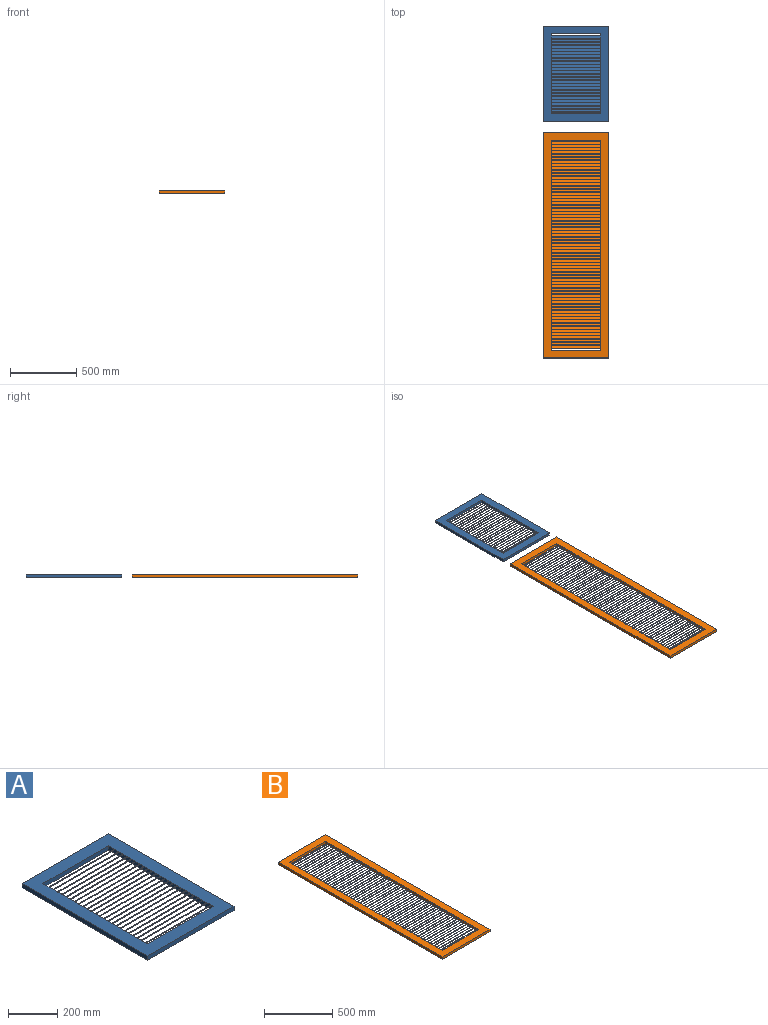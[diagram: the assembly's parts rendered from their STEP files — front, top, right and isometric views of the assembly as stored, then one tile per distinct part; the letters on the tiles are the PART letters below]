
ASSEMBLY  parts=2 mates=2
PART A: 106 faces, bbox 494x720x21 mm
  f0: plane 600x21mm, normal (1,0,0), area 10776mm2, adj f2,f7,f8,f9,f10,f11,f12,f13
  f1: plane 600x21mm, normal (-1,0,0), area 10776mm2, adj f2,f7,f8,f9,f10,f11,f12,f13
  f2: plane 374x21mm, normal (0,-1,0), area 7854mm2, adj f0,f1,f8,f9
  f3: plane 494x21mm, normal (0,1,0), area 10374mm2, adj f4,f6,f8,f9
  f4: plane 720x21mm, normal (-1,0,0), area 15120mm2, adj f3,f5,f8,f9
  f5: plane 494x21mm, normal (0,-1,0), area 10374mm2, adj f4,f6,f8,f9
  f6: plane 720x21mm, normal (1,0,0), area 15120mm2, adj f3,f5,f8,f9
  f7: plane 374x21mm, normal (0,1,0), area 7854mm2, adj f0,f1,f8,f9
  f8: plane 720x494mm, normal (0,0,1), area 131280mm2, adj f0,f1,f2,f3,f4,f5,f6,f7
  f9: plane 720x494mm, normal (0,0,-1), area 131280mm2, adj f0,f1,f2,f3,f4,f5,f6,f7
  f10: plane 374x19mm, normal (0,-0.71,-0.71), area 10049.4mm2, adj f0,f1,f11,f13
  f11: plane 374x4mm, normal (0,0,-1), area 1496mm2, adj f0,f1,f10,f12
  f12: plane 374x19mm, normal (0,0.71,0.71), area 10049.4mm2, adj f0,f1,f11,f13
  f13: plane 374x4mm, normal (0,0,1), area 1496mm2, adj f0,f1,f10,f12
  f14: plane 374x19mm, normal (0,-0.71,-0.71), area 10049.4mm2, adj f0,f1,f15,f17
  f15: plane 374x4mm, normal (0,0,-1), area 1496mm2, adj f0,f1,f14,f16
  f16: plane 374x19mm, normal (0,0.71,0.71), area 10049.4mm2, adj f0,f1,f15,f17
  f17: plane 374x4mm, normal (0,0,1), area 1496mm2, adj f0,f1,f14,f16
  f18: plane 374x19mm, normal (0,-0.71,-0.71), area 10049.4mm2, adj f0,f1,f19,f21
  f19: plane 374x4mm, normal (0,0,-1), area 1496mm2, adj f0,f1,f18,f20
  f20: plane 374x19mm, normal (0,0.71,0.71), area 10049.4mm2, adj f0,f1,f19,f21
  f21: plane 374x4mm, normal (0,0,1), area 1496mm2, adj f0,f1,f18,f20
  f22: plane 374x19mm, normal (0,-0.71,-0.71), area 10049.4mm2, adj f0,f1,f23,f25
  f23: plane 374x4mm, normal (0,0,-1), area 1496mm2, adj f0,f1,f22,f24
  f24: plane 374x19mm, normal (0,0.71,0.71), area 10049.4mm2, adj f0,f1,f23,f25
  f25: plane 374x4mm, normal (0,0,1), area 1496mm2, adj f0,f1,f22,f24
  f26: plane 374x19mm, normal (0,-0.71,-0.71), area 10049.4mm2, adj f0,f1,f27,f29
  f27: plane 374x4mm, normal (0,0,-1), area 1496mm2, adj f0,f1,f26,f28
  f28: plane 374x19mm, normal (0,0.71,0.71), area 10049.4mm2, adj f0,f1,f27,f29
  f29: plane 374x4mm, normal (0,0,1), area 1496mm2, adj f0,f1,f26,f28
  f30: plane 374x19mm, normal (0,-0.71,-0.71), area 10049.4mm2, adj f0,f1,f31,f33
  f31: plane 374x4mm, normal (0,0,-1), area 1496mm2, adj f0,f1,f30,f32
  f32: plane 374x19mm, normal (0,0.71,0.71), area 10049.4mm2, adj f0,f1,f31,f33
  f33: plane 374x4mm, normal (0,0,1), area 1496mm2, adj f0,f1,f30,f32
  f34: plane 374x19mm, normal (0,-0.71,-0.71), area 10049.4mm2, adj f0,f1,f35,f37
  f35: plane 374x4mm, normal (0,0,-1), area 1496mm2, adj f0,f1,f34,f36
  f36: plane 374x19mm, normal (0,0.71,0.71), area 10049.4mm2, adj f0,f1,f35,f37
  f37: plane 374x4mm, normal (0,0,1), area 1496mm2, adj f0,f1,f34,f36
  f38: plane 374x19mm, normal (0,-0.71,-0.71), area 10049.4mm2, adj f0,f1,f39,f41
  f39: plane 374x4mm, normal (0,0,-1), area 1496mm2, adj f0,f1,f38,f40
  f40: plane 374x19mm, normal (0,0.71,0.71), area 10049.4mm2, adj f0,f1,f39,f41
  f41: plane 374x4mm, normal (0,0,1), area 1496mm2, adj f0,f1,f38,f40
  f42: plane 374x19mm, normal (0,-0.71,-0.71), area 10049.4mm2, adj f0,f1,f43,f45
  f43: plane 374x4mm, normal (0,0,-1), area 1496mm2, adj f0,f1,f42,f44
  f44: plane 374x19mm, normal (0,0.71,0.71), area 10049.4mm2, adj f0,f1,f43,f45
  f45: plane 374x4mm, normal (0,0,1), area 1496mm2, adj f0,f1,f42,f44
  f46: plane 374x19mm, normal (0,-0.71,-0.71), area 10049.4mm2, adj f0,f1,f47,f49
  f47: plane 374x4mm, normal (0,0,-1), area 1496mm2, adj f0,f1,f46,f48
  f48: plane 374x19mm, normal (0,0.71,0.71), area 10049.4mm2, adj f0,f1,f47,f49
  f49: plane 374x4mm, normal (0,0,1), area 1496mm2, adj f0,f1,f46,f48
  f50: plane 374x19mm, normal (0,-0.71,-0.71), area 10049.4mm2, adj f0,f1,f51,f53
  f51: plane 374x4mm, normal (0,0,-1), area 1496mm2, adj f0,f1,f50,f52
  f52: plane 374x19mm, normal (0,0.71,0.71), area 10049.4mm2, adj f0,f1,f51,f53
  f53: plane 374x4mm, normal (0,0,1), area 1496mm2, adj f0,f1,f50,f52
  f54: plane 374x19mm, normal (0,-0.71,-0.71), area 10049.4mm2, adj f0,f1,f55,f57
  f55: plane 374x4mm, normal (0,0,-1), area 1496mm2, adj f0,f1,f54,f56
  f56: plane 374x19mm, normal (0,0.71,0.71), area 10049.4mm2, adj f0,f1,f55,f57
  f57: plane 374x4mm, normal (0,0,1), area 1496mm2, adj f0,f1,f54,f56
  f58: plane 374x19mm, normal (0,-0.71,-0.71), area 10049.4mm2, adj f0,f1,f59,f61
  f59: plane 374x4mm, normal (0,0,-1), area 1496mm2, adj f0,f1,f58,f60
  f60: plane 374x19mm, normal (0,0.71,0.71), area 10049.4mm2, adj f0,f1,f59,f61
  f61: plane 374x4mm, normal (0,0,1), area 1496mm2, adj f0,f1,f58,f60
  f62: plane 374x19mm, normal (0,-0.71,-0.71), area 10049.4mm2, adj f0,f1,f63,f65
  f63: plane 374x4mm, normal (0,0,-1), area 1496mm2, adj f0,f1,f62,f64
  f64: plane 374x19mm, normal (0,0.71,0.71), area 10049.4mm2, adj f0,f1,f63,f65
  f65: plane 374x4mm, normal (0,0,1), area 1496mm2, adj f0,f1,f62,f64
  f66: plane 374x19mm, normal (0,-0.71,-0.71), area 10049.4mm2, adj f0,f1,f67,f69
  f67: plane 374x4mm, normal (0,0,-1), area 1496mm2, adj f0,f1,f66,f68
  f68: plane 374x19mm, normal (0,0.71,0.71), area 10049.4mm2, adj f0,f1,f67,f69
  f69: plane 374x4mm, normal (0,0,1), area 1496mm2, adj f0,f1,f66,f68
  f70: plane 374x19mm, normal (0,-0.71,-0.71), area 10049.4mm2, adj f0,f1,f71,f73
  f71: plane 374x4mm, normal (0,0,-1), area 1496mm2, adj f0,f1,f70,f72
  f72: plane 374x19mm, normal (0,0.71,0.71), area 10049.4mm2, adj f0,f1,f71,f73
  f73: plane 374x4mm, normal (0,0,1), area 1496mm2, adj f0,f1,f70,f72
  f74: plane 374x19mm, normal (0,-0.71,-0.71), area 10049.4mm2, adj f0,f1,f75,f77
  f75: plane 374x4mm, normal (0,0,-1), area 1496mm2, adj f0,f1,f74,f76
  f76: plane 374x19mm, normal (0,0.71,0.71), area 10049.4mm2, adj f0,f1,f75,f77
  f77: plane 374x4mm, normal (0,0,1), area 1496mm2, adj f0,f1,f74,f76
  f78: plane 374x19mm, normal (0,-0.71,-0.71), area 10049.4mm2, adj f0,f1,f79,f81
  f79: plane 374x4mm, normal (0,0,-1), area 1496mm2, adj f0,f1,f78,f80
  f80: plane 374x19mm, normal (0,0.71,0.71), area 10049.4mm2, adj f0,f1,f79,f81
  f81: plane 374x4mm, normal (0,0,1), area 1496mm2, adj f0,f1,f78,f80
  f82: plane 374x19mm, normal (0,-0.71,-0.71), area 10049.4mm2, adj f0,f1,f83,f85
  f83: plane 374x4mm, normal (0,0,-1), area 1496mm2, adj f0,f1,f82,f84
  f84: plane 374x19mm, normal (0,0.71,0.71), area 10049.4mm2, adj f0,f1,f83,f85
  f85: plane 374x4mm, normal (0,0,1), area 1496mm2, adj f0,f1,f82,f84
  f86: plane 374x19mm, normal (0,-0.71,-0.71), area 10049.4mm2, adj f0,f1,f87,f89
  f87: plane 374x4mm, normal (0,0,-1), area 1496mm2, adj f0,f1,f86,f88
  f88: plane 374x19mm, normal (0,0.71,0.71), area 10049.4mm2, adj f0,f1,f87,f89
  f89: plane 374x4mm, normal (0,0,1), area 1496mm2, adj f0,f1,f86,f88
  f90: plane 374x19mm, normal (0,-0.71,-0.71), area 10049.4mm2, adj f0,f1,f91,f93
  f91: plane 374x4mm, normal (0,0,-1), area 1496mm2, adj f0,f1,f90,f92
  f92: plane 374x19mm, normal (0,0.71,0.71), area 10049.4mm2, adj f0,f1,f91,f93
  f93: plane 374x4mm, normal (0,0,1), area 1496mm2, adj f0,f1,f90,f92
  f94: plane 374x19mm, normal (0,-0.71,-0.71), area 10049.4mm2, adj f0,f1,f95,f97
  f95: plane 374x4mm, normal (0,0,-1), area 1496mm2, adj f0,f1,f94,f96
  f96: plane 374x19mm, normal (0,0.71,0.71), area 10049.4mm2, adj f0,f1,f95,f97
  f97: plane 374x4mm, normal (0,0,1), area 1496mm2, adj f0,f1,f94,f96
  f98: plane 374x19mm, normal (0,-0.71,-0.71), area 10049.4mm2, adj f0,f1,f99,f101
  f99: plane 374x4mm, normal (0,0,-1), area 1496mm2, adj f0,f1,f98,f100
  f100: plane 374x19mm, normal (0,0.71,0.71), area 10049.4mm2, adj f0,f1,f99,f101
  f101: plane 374x4mm, normal (0,0,1), area 1496mm2, adj f0,f1,f98,f100
  f102: plane 374x19mm, normal (0,-0.71,-0.71), area 10049.4mm2, adj f0,f1,f103,f105
  f103: plane 374x4mm, normal (0,0,-1), area 1496mm2, adj f0,f1,f102,f104
  f104: plane 374x19mm, normal (0,0.71,0.71), area 10049.4mm2, adj f0,f1,f103,f105
  f105: plane 374x4mm, normal (0,0,1), area 1496mm2, adj f0,f1,f102,f104
PART B: 270 faces, bbox 494x1700x21 mm
  f0: plane 1580x21mm, normal (1,0,0), area 28240mm2, adj f2,f7,f8,f9,f10,f11,f12,f13
  f1: plane 1580x21mm, normal (-1,0,0), area 28240mm2, adj f2,f7,f8,f9,f10,f11,f12,f13
  f2: plane 374x21mm, normal (0,-1,0), area 7854mm2, adj f0,f1,f8,f9
  f3: plane 494x21mm, normal (0,1,0), area 10374mm2, adj f4,f6,f8,f9
  f4: plane 1700x21mm, normal (-1,0,0), area 35700mm2, adj f3,f5,f8,f9
  f5: plane 494x21mm, normal (0,-1,0), area 10374mm2, adj f4,f6,f8,f9
  f6: plane 1700x21mm, normal (1,0,0), area 35700mm2, adj f3,f5,f8,f9
  f7: plane 374x21mm, normal (0,1,0), area 7854mm2, adj f0,f1,f8,f9
  f8: plane 1700x494mm, normal (0,0,1), area 248880mm2, adj f0,f1,f2,f3,f4,f5,f6,f7
  f9: plane 1700x494mm, normal (0,0,-1), area 248880mm2, adj f0,f1,f2,f3,f4,f5,f6,f7
  f10: plane 374x19mm, normal (0,-0.71,-0.71), area 10049.4mm2, adj f0,f1,f11,f13
  f11: plane 374x4mm, normal (0,0,-1), area 1496mm2, adj f0,f1,f10,f12
  f12: plane 374x19mm, normal (0,0.71,0.71), area 10049.4mm2, adj f0,f1,f11,f13
  f13: plane 374x4mm, normal (0,0,1), area 1496mm2, adj f0,f1,f10,f12
  f14: plane 374x19mm, normal (0,-0.71,-0.71), area 10049.4mm2, adj f0,f1,f15,f17
  f15: plane 374x4mm, normal (0,0,-1), area 1496mm2, adj f0,f1,f14,f16
  f16: plane 374x19mm, normal (0,0.71,0.71), area 10049.4mm2, adj f0,f1,f15,f17
  f17: plane 374x4mm, normal (0,0,1), area 1496mm2, adj f0,f1,f14,f16
  f18: plane 374x19mm, normal (0,-0.71,-0.71), area 10049.4mm2, adj f0,f1,f19,f21
  f19: plane 374x4mm, normal (0,0,-1), area 1496mm2, adj f0,f1,f18,f20
  f20: plane 374x19mm, normal (0,0.71,0.71), area 10049.4mm2, adj f0,f1,f19,f21
  f21: plane 374x4mm, normal (0,0,1), area 1496mm2, adj f0,f1,f18,f20
  f22: plane 374x19mm, normal (0,-0.71,-0.71), area 10049.4mm2, adj f0,f1,f23,f25
  f23: plane 374x4mm, normal (0,0,-1), area 1496mm2, adj f0,f1,f22,f24
  f24: plane 374x19mm, normal (0,0.71,0.71), area 10049.4mm2, adj f0,f1,f23,f25
  f25: plane 374x4mm, normal (0,0,1), area 1496mm2, adj f0,f1,f22,f24
  f26: plane 374x19mm, normal (0,-0.71,-0.71), area 10049.4mm2, adj f0,f1,f27,f29
  f27: plane 374x4mm, normal (0,0,-1), area 1496mm2, adj f0,f1,f26,f28
  f28: plane 374x19mm, normal (0,0.71,0.71), area 10049.4mm2, adj f0,f1,f27,f29
  f29: plane 374x4mm, normal (0,0,1), area 1496mm2, adj f0,f1,f26,f28
  f30: plane 374x19mm, normal (0,-0.71,-0.71), area 10049.4mm2, adj f0,f1,f31,f33
  f31: plane 374x4mm, normal (0,0,-1), area 1496mm2, adj f0,f1,f30,f32
  f32: plane 374x19mm, normal (0,0.71,0.71), area 10049.4mm2, adj f0,f1,f31,f33
  f33: plane 374x4mm, normal (0,0,1), area 1496mm2, adj f0,f1,f30,f32
  f34: plane 374x19mm, normal (0,-0.71,-0.71), area 10049.4mm2, adj f0,f1,f35,f37
  f35: plane 374x4mm, normal (0,0,-1), area 1496mm2, adj f0,f1,f34,f36
  f36: plane 374x19mm, normal (0,0.71,0.71), area 10049.4mm2, adj f0,f1,f35,f37
  f37: plane 374x4mm, normal (0,0,1), area 1496mm2, adj f0,f1,f34,f36
  f38: plane 374x19mm, normal (0,-0.71,-0.71), area 10049.4mm2, adj f0,f1,f39,f41
  f39: plane 374x4mm, normal (0,0,-1), area 1496mm2, adj f0,f1,f38,f40
  f40: plane 374x19mm, normal (0,0.71,0.71), area 10049.4mm2, adj f0,f1,f39,f41
  f41: plane 374x4mm, normal (0,0,1), area 1496mm2, adj f0,f1,f38,f40
  f42: plane 374x19mm, normal (0,-0.71,-0.71), area 10049.4mm2, adj f0,f1,f43,f45
  f43: plane 374x4mm, normal (0,0,-1), area 1496mm2, adj f0,f1,f42,f44
  f44: plane 374x19mm, normal (0,0.71,0.71), area 10049.4mm2, adj f0,f1,f43,f45
  f45: plane 374x4mm, normal (0,0,1), area 1496mm2, adj f0,f1,f42,f44
  f46: plane 374x19mm, normal (0,-0.71,-0.71), area 10049.4mm2, adj f0,f1,f47,f49
  f47: plane 374x4mm, normal (0,0,-1), area 1496mm2, adj f0,f1,f46,f48
  f48: plane 374x19mm, normal (0,0.71,0.71), area 10049.4mm2, adj f0,f1,f47,f49
  f49: plane 374x4mm, normal (0,0,1), area 1496mm2, adj f0,f1,f46,f48
  f50: plane 374x19mm, normal (0,-0.71,-0.71), area 10049.4mm2, adj f0,f1,f51,f53
  f51: plane 374x4mm, normal (0,0,-1), area 1496mm2, adj f0,f1,f50,f52
  f52: plane 374x19mm, normal (0,0.71,0.71), area 10049.4mm2, adj f0,f1,f51,f53
  f53: plane 374x4mm, normal (0,0,1), area 1496mm2, adj f0,f1,f50,f52
  f54: plane 374x19mm, normal (0,-0.71,-0.71), area 10049.4mm2, adj f0,f1,f55,f57
  f55: plane 374x4mm, normal (0,0,-1), area 1496mm2, adj f0,f1,f54,f56
  f56: plane 374x19mm, normal (0,0.71,0.71), area 10049.4mm2, adj f0,f1,f55,f57
  f57: plane 374x4mm, normal (0,0,1), area 1496mm2, adj f0,f1,f54,f56
  f58: plane 374x19mm, normal (0,-0.71,-0.71), area 10049.4mm2, adj f0,f1,f59,f61
  f59: plane 374x4mm, normal (0,0,-1), area 1496mm2, adj f0,f1,f58,f60
  f60: plane 374x19mm, normal (0,0.71,0.71), area 10049.4mm2, adj f0,f1,f59,f61
  f61: plane 374x4mm, normal (0,0,1), area 1496mm2, adj f0,f1,f58,f60
  f62: plane 374x19mm, normal (0,-0.71,-0.71), area 10049.4mm2, adj f0,f1,f63,f65
  f63: plane 374x4mm, normal (0,0,-1), area 1496mm2, adj f0,f1,f62,f64
  f64: plane 374x19mm, normal (0,0.71,0.71), area 10049.4mm2, adj f0,f1,f63,f65
  f65: plane 374x4mm, normal (0,0,1), area 1496mm2, adj f0,f1,f62,f64
  f66: plane 374x19mm, normal (0,-0.71,-0.71), area 10049.4mm2, adj f0,f1,f67,f69
  f67: plane 374x4mm, normal (0,0,-1), area 1496mm2, adj f0,f1,f66,f68
  f68: plane 374x19mm, normal (0,0.71,0.71), area 10049.4mm2, adj f0,f1,f67,f69
  f69: plane 374x4mm, normal (0,0,1), area 1496mm2, adj f0,f1,f66,f68
  f70: plane 374x19mm, normal (0,-0.71,-0.71), area 10049.4mm2, adj f0,f1,f71,f73
  f71: plane 374x4mm, normal (0,0,-1), area 1496mm2, adj f0,f1,f70,f72
  f72: plane 374x19mm, normal (0,0.71,0.71), area 10049.4mm2, adj f0,f1,f71,f73
  f73: plane 374x4mm, normal (0,0,1), area 1496mm2, adj f0,f1,f70,f72
  f74: plane 374x19mm, normal (0,-0.71,-0.71), area 10049.4mm2, adj f0,f1,f75,f77
  f75: plane 374x4mm, normal (0,0,-1), area 1496mm2, adj f0,f1,f74,f76
  f76: plane 374x19mm, normal (0,0.71,0.71), area 10049.4mm2, adj f0,f1,f75,f77
  f77: plane 374x4mm, normal (0,0,1), area 1496mm2, adj f0,f1,f74,f76
  f78: plane 374x19mm, normal (0,-0.71,-0.71), area 10049.4mm2, adj f0,f1,f79,f81
  f79: plane 374x4mm, normal (0,0,-1), area 1496mm2, adj f0,f1,f78,f80
  f80: plane 374x19mm, normal (0,0.71,0.71), area 10049.4mm2, adj f0,f1,f79,f81
  f81: plane 374x4mm, normal (0,0,1), area 1496mm2, adj f0,f1,f78,f80
  f82: plane 374x19mm, normal (0,-0.71,-0.71), area 10049.4mm2, adj f0,f1,f83,f85
  f83: plane 374x4mm, normal (0,0,-1), area 1496mm2, adj f0,f1,f82,f84
  f84: plane 374x19mm, normal (0,0.71,0.71), area 10049.4mm2, adj f0,f1,f83,f85
  f85: plane 374x4mm, normal (0,0,1), area 1496mm2, adj f0,f1,f82,f84
  f86: plane 374x19mm, normal (0,-0.71,-0.71), area 10049.4mm2, adj f0,f1,f87,f89
  f87: plane 374x4mm, normal (0,0,-1), area 1496mm2, adj f0,f1,f86,f88
  f88: plane 374x19mm, normal (0,0.71,0.71), area 10049.4mm2, adj f0,f1,f87,f89
  f89: plane 374x4mm, normal (0,0,1), area 1496mm2, adj f0,f1,f86,f88
  f90: plane 374x19mm, normal (0,-0.71,-0.71), area 10049.4mm2, adj f0,f1,f91,f93
  f91: plane 374x4mm, normal (0,0,-1), area 1496mm2, adj f0,f1,f90,f92
  f92: plane 374x19mm, normal (0,0.71,0.71), area 10049.4mm2, adj f0,f1,f91,f93
  f93: plane 374x4mm, normal (0,0,1), area 1496mm2, adj f0,f1,f90,f92
  f94: plane 374x19mm, normal (0,-0.71,-0.71), area 10049.4mm2, adj f0,f1,f95,f97
  f95: plane 374x4mm, normal (0,0,-1), area 1496mm2, adj f0,f1,f94,f96
  f96: plane 374x19mm, normal (0,0.71,0.71), area 10049.4mm2, adj f0,f1,f95,f97
  f97: plane 374x4mm, normal (0,0,1), area 1496mm2, adj f0,f1,f94,f96
  f98: plane 374x19mm, normal (0,-0.71,-0.71), area 10049.4mm2, adj f0,f1,f99,f101
  f99: plane 374x4mm, normal (0,0,-1), area 1496mm2, adj f0,f1,f98,f100
  f100: plane 374x19mm, normal (0,0.71,0.71), area 10049.4mm2, adj f0,f1,f99,f101
  f101: plane 374x4mm, normal (0,0,1), area 1496mm2, adj f0,f1,f98,f100
  f102: plane 374x19mm, normal (0,-0.71,-0.71), area 10049.4mm2, adj f0,f1,f103,f105
  f103: plane 374x4mm, normal (0,0,-1), area 1496mm2, adj f0,f1,f102,f104
  f104: plane 374x19mm, normal (0,0.71,0.71), area 10049.4mm2, adj f0,f1,f103,f105
  f105: plane 374x4mm, normal (0,0,1), area 1496mm2, adj f0,f1,f102,f104
  f106: plane 374x19mm, normal (0,-0.71,-0.71), area 10049.4mm2, adj f0,f1,f107,f109
  f107: plane 374x4mm, normal (0,0,-1), area 1496mm2, adj f0,f1,f106,f108
  f108: plane 374x19mm, normal (0,0.71,0.71), area 10049.4mm2, adj f0,f1,f107,f109
  f109: plane 374x4mm, normal (0,0,1), area 1496mm2, adj f0,f1,f106,f108
  f110: plane 374x19mm, normal (0,-0.71,-0.71), area 10049.4mm2, adj f0,f1,f111,f113
  f111: plane 374x4mm, normal (0,0,-1), area 1496mm2, adj f0,f1,f110,f112
  f112: plane 374x19mm, normal (0,0.71,0.71), area 10049.4mm2, adj f0,f1,f111,f113
  f113: plane 374x4mm, normal (0,0,1), area 1496mm2, adj f0,f1,f110,f112
  f114: plane 374x19mm, normal (0,-0.71,-0.71), area 10049.4mm2, adj f0,f1,f115,f117
  f115: plane 374x4mm, normal (0,0,-1), area 1496mm2, adj f0,f1,f114,f116
  f116: plane 374x19mm, normal (0,0.71,0.71), area 10049.4mm2, adj f0,f1,f115,f117
  f117: plane 374x4mm, normal (0,0,1), area 1496mm2, adj f0,f1,f114,f116
  f118: plane 374x19mm, normal (0,-0.71,-0.71), area 10049.4mm2, adj f0,f1,f119,f121
  f119: plane 374x4mm, normal (0,0,-1), area 1496mm2, adj f0,f1,f118,f120
  f120: plane 374x19mm, normal (0,0.71,0.71), area 10049.4mm2, adj f0,f1,f119,f121
  f121: plane 374x4mm, normal (0,0,1), area 1496mm2, adj f0,f1,f118,f120
  f122: plane 374x19mm, normal (0,-0.71,-0.71), area 10049.4mm2, adj f0,f1,f123,f125
  f123: plane 374x4mm, normal (0,0,-1), area 1496mm2, adj f0,f1,f122,f124
  f124: plane 374x19mm, normal (0,0.71,0.71), area 10049.4mm2, adj f0,f1,f123,f125
  f125: plane 374x4mm, normal (0,0,1), area 1496mm2, adj f0,f1,f122,f124
  f126: plane 374x19mm, normal (0,-0.71,-0.71), area 10049.4mm2, adj f0,f1,f127,f129
  f127: plane 374x4mm, normal (0,0,-1), area 1496mm2, adj f0,f1,f126,f128
  f128: plane 374x19mm, normal (0,0.71,0.71), area 10049.4mm2, adj f0,f1,f127,f129
  f129: plane 374x4mm, normal (0,0,1), area 1496mm2, adj f0,f1,f126,f128
  f130: plane 374x19mm, normal (0,-0.71,-0.71), area 10049.4mm2, adj f0,f1,f131,f133
  f131: plane 374x4mm, normal (0,0,-1), area 1496mm2, adj f0,f1,f130,f132
  f132: plane 374x19mm, normal (0,0.71,0.71), area 10049.4mm2, adj f0,f1,f131,f133
  f133: plane 374x4mm, normal (0,0,1), area 1496mm2, adj f0,f1,f130,f132
  f134: plane 374x19mm, normal (0,-0.71,-0.71), area 10049.4mm2, adj f0,f1,f135,f137
  f135: plane 374x4mm, normal (0,0,-1), area 1496mm2, adj f0,f1,f134,f136
  f136: plane 374x19mm, normal (0,0.71,0.71), area 10049.4mm2, adj f0,f1,f135,f137
  f137: plane 374x4mm, normal (0,0,1), area 1496mm2, adj f0,f1,f134,f136
  f138: plane 374x19mm, normal (0,-0.71,-0.71), area 10049.4mm2, adj f0,f1,f139,f141
  f139: plane 374x4mm, normal (0,0,-1), area 1496mm2, adj f0,f1,f138,f140
  f140: plane 374x19mm, normal (0,0.71,0.71), area 10049.4mm2, adj f0,f1,f139,f141
  f141: plane 374x4mm, normal (0,0,1), area 1496mm2, adj f0,f1,f138,f140
  f142: plane 374x19mm, normal (0,-0.71,-0.71), area 10049.4mm2, adj f0,f1,f143,f145
  f143: plane 374x4mm, normal (0,0,-1), area 1496mm2, adj f0,f1,f142,f144
  f144: plane 374x19mm, normal (0,0.71,0.71), area 10049.4mm2, adj f0,f1,f143,f145
  f145: plane 374x4mm, normal (0,0,1), area 1496mm2, adj f0,f1,f142,f144
  f146: plane 374x19mm, normal (0,-0.71,-0.71), area 10049.4mm2, adj f0,f1,f147,f149
  f147: plane 374x4mm, normal (0,0,-1), area 1496mm2, adj f0,f1,f146,f148
  f148: plane 374x19mm, normal (0,0.71,0.71), area 10049.4mm2, adj f0,f1,f147,f149
  f149: plane 374x4mm, normal (0,0,1), area 1496mm2, adj f0,f1,f146,f148
  f150: plane 374x19mm, normal (0,-0.71,-0.71), area 10049.4mm2, adj f0,f1,f151,f153
  f151: plane 374x4mm, normal (0,0,-1), area 1496mm2, adj f0,f1,f150,f152
  f152: plane 374x19mm, normal (0,0.71,0.71), area 10049.4mm2, adj f0,f1,f151,f153
  f153: plane 374x4mm, normal (0,0,1), area 1496mm2, adj f0,f1,f150,f152
  f154: plane 374x19mm, normal (0,-0.71,-0.71), area 10049.4mm2, adj f0,f1,f155,f157
  f155: plane 374x4mm, normal (0,0,-1), area 1496mm2, adj f0,f1,f154,f156
  f156: plane 374x19mm, normal (0,0.71,0.71), area 10049.4mm2, adj f0,f1,f155,f157
  f157: plane 374x4mm, normal (0,0,1), area 1496mm2, adj f0,f1,f154,f156
  f158: plane 374x19mm, normal (0,-0.71,-0.71), area 10049.4mm2, adj f0,f1,f159,f161
  f159: plane 374x4mm, normal (0,0,-1), area 1496mm2, adj f0,f1,f158,f160
  f160: plane 374x19mm, normal (0,0.71,0.71), area 10049.4mm2, adj f0,f1,f159,f161
  f161: plane 374x4mm, normal (0,0,1), area 1496mm2, adj f0,f1,f158,f160
  f162: plane 374x19mm, normal (0,-0.71,-0.71), area 10049.4mm2, adj f0,f1,f163,f165
  f163: plane 374x4mm, normal (0,0,-1), area 1496mm2, adj f0,f1,f162,f164
  f164: plane 374x19mm, normal (0,0.71,0.71), area 10049.4mm2, adj f0,f1,f163,f165
  f165: plane 374x4mm, normal (0,0,1), area 1496mm2, adj f0,f1,f162,f164
  f166: plane 374x19mm, normal (0,-0.71,-0.71), area 10049.4mm2, adj f0,f1,f167,f169
  f167: plane 374x4mm, normal (0,0,-1), area 1496mm2, adj f0,f1,f166,f168
  f168: plane 374x19mm, normal (0,0.71,0.71), area 10049.4mm2, adj f0,f1,f167,f169
  f169: plane 374x4mm, normal (0,0,1), area 1496mm2, adj f0,f1,f166,f168
  f170: plane 374x19mm, normal (0,-0.71,-0.71), area 10049.4mm2, adj f0,f1,f171,f173
  f171: plane 374x4mm, normal (0,0,-1), area 1496mm2, adj f0,f1,f170,f172
  f172: plane 374x19mm, normal (0,0.71,0.71), area 10049.4mm2, adj f0,f1,f171,f173
  f173: plane 374x4mm, normal (0,0,1), area 1496mm2, adj f0,f1,f170,f172
  f174: plane 374x19mm, normal (0,-0.71,-0.71), area 10049.4mm2, adj f0,f1,f175,f177
  f175: plane 374x4mm, normal (0,0,-1), area 1496mm2, adj f0,f1,f174,f176
  f176: plane 374x19mm, normal (0,0.71,0.71), area 10049.4mm2, adj f0,f1,f175,f177
  f177: plane 374x4mm, normal (0,0,1), area 1496mm2, adj f0,f1,f174,f176
  f178: plane 374x19mm, normal (0,-0.71,-0.71), area 10049.4mm2, adj f0,f1,f179,f181
  f179: plane 374x4mm, normal (0,0,-1), area 1496mm2, adj f0,f1,f178,f180
  f180: plane 374x19mm, normal (0,0.71,0.71), area 10049.4mm2, adj f0,f1,f179,f181
  f181: plane 374x4mm, normal (0,0,1), area 1496mm2, adj f0,f1,f178,f180
  f182: plane 374x19mm, normal (0,-0.71,-0.71), area 10049.4mm2, adj f0,f1,f183,f185
  f183: plane 374x4mm, normal (0,0,-1), area 1496mm2, adj f0,f1,f182,f184
  f184: plane 374x19mm, normal (0,0.71,0.71), area 10049.4mm2, adj f0,f1,f183,f185
  f185: plane 374x4mm, normal (0,0,1), area 1496mm2, adj f0,f1,f182,f184
  f186: plane 374x19mm, normal (0,-0.71,-0.71), area 10049.4mm2, adj f0,f1,f187,f189
  f187: plane 374x4mm, normal (0,0,-1), area 1496mm2, adj f0,f1,f186,f188
  f188: plane 374x19mm, normal (0,0.71,0.71), area 10049.4mm2, adj f0,f1,f187,f189
  f189: plane 374x4mm, normal (0,0,1), area 1496mm2, adj f0,f1,f186,f188
  f190: plane 374x19mm, normal (0,-0.71,-0.71), area 10049.4mm2, adj f0,f1,f191,f193
  f191: plane 374x4mm, normal (0,0,-1), area 1496mm2, adj f0,f1,f190,f192
  f192: plane 374x19mm, normal (0,0.71,0.71), area 10049.4mm2, adj f0,f1,f191,f193
  f193: plane 374x4mm, normal (0,0,1), area 1496mm2, adj f0,f1,f190,f192
  f194: plane 374x19mm, normal (0,-0.71,-0.71), area 10049.4mm2, adj f0,f1,f195,f197
  f195: plane 374x4mm, normal (0,0,-1), area 1496mm2, adj f0,f1,f194,f196
  f196: plane 374x19mm, normal (0,0.71,0.71), area 10049.4mm2, adj f0,f1,f195,f197
  f197: plane 374x4mm, normal (0,0,1), area 1496mm2, adj f0,f1,f194,f196
  f198: plane 374x19mm, normal (0,-0.71,-0.71), area 10049.4mm2, adj f0,f1,f199,f201
  f199: plane 374x4mm, normal (0,0,-1), area 1496mm2, adj f0,f1,f198,f200
  f200: plane 374x19mm, normal (0,0.71,0.71), area 10049.4mm2, adj f0,f1,f199,f201
  f201: plane 374x4mm, normal (0,0,1), area 1496mm2, adj f0,f1,f198,f200
  f202: plane 374x19mm, normal (0,-0.71,-0.71), area 10049.4mm2, adj f0,f1,f203,f205
  f203: plane 374x4mm, normal (0,0,-1), area 1496mm2, adj f0,f1,f202,f204
  f204: plane 374x19mm, normal (0,0.71,0.71), area 10049.4mm2, adj f0,f1,f203,f205
  f205: plane 374x4mm, normal (0,0,1), area 1496mm2, adj f0,f1,f202,f204
  f206: plane 374x19mm, normal (0,-0.71,-0.71), area 10049.4mm2, adj f0,f1,f207,f209
  f207: plane 374x4mm, normal (0,0,-1), area 1496mm2, adj f0,f1,f206,f208
  f208: plane 374x19mm, normal (0,0.71,0.71), area 10049.4mm2, adj f0,f1,f207,f209
  f209: plane 374x4mm, normal (0,0,1), area 1496mm2, adj f0,f1,f206,f208
  f210: plane 374x19mm, normal (0,-0.71,-0.71), area 10049.4mm2, adj f0,f1,f211,f213
  f211: plane 374x4mm, normal (0,0,-1), area 1496mm2, adj f0,f1,f210,f212
  f212: plane 374x19mm, normal (0,0.71,0.71), area 10049.4mm2, adj f0,f1,f211,f213
  f213: plane 374x4mm, normal (0,0,1), area 1496mm2, adj f0,f1,f210,f212
  f214: plane 374x19mm, normal (0,-0.71,-0.71), area 10049.4mm2, adj f0,f1,f215,f217
  f215: plane 374x4mm, normal (0,0,-1), area 1496mm2, adj f0,f1,f214,f216
  f216: plane 374x19mm, normal (0,0.71,0.71), area 10049.4mm2, adj f0,f1,f215,f217
  f217: plane 374x4mm, normal (0,0,1), area 1496mm2, adj f0,f1,f214,f216
  f218: plane 374x19mm, normal (0,-0.71,-0.71), area 10049.4mm2, adj f0,f1,f219,f221
  f219: plane 374x4mm, normal (0,0,-1), area 1496mm2, adj f0,f1,f218,f220
  f220: plane 374x19mm, normal (0,0.71,0.71), area 10049.4mm2, adj f0,f1,f219,f221
  f221: plane 374x4mm, normal (0,0,1), area 1496mm2, adj f0,f1,f218,f220
  f222: plane 374x19mm, normal (0,-0.71,-0.71), area 10049.4mm2, adj f0,f1,f223,f225
  f223: plane 374x4mm, normal (0,0,-1), area 1496mm2, adj f0,f1,f222,f224
  f224: plane 374x19mm, normal (0,0.71,0.71), area 10049.4mm2, adj f0,f1,f223,f225
  f225: plane 374x4mm, normal (0,0,1), area 1496mm2, adj f0,f1,f222,f224
  f226: plane 374x19mm, normal (0,-0.71,-0.71), area 10049.4mm2, adj f0,f1,f227,f229
  f227: plane 374x4mm, normal (0,0,-1), area 1496mm2, adj f0,f1,f226,f228
  f228: plane 374x19mm, normal (0,0.71,0.71), area 10049.4mm2, adj f0,f1,f227,f229
  f229: plane 374x4mm, normal (0,0,1), area 1496mm2, adj f0,f1,f226,f228
  f230: plane 374x19mm, normal (0,-0.71,-0.71), area 10049.4mm2, adj f0,f1,f231,f233
  f231: plane 374x4mm, normal (0,0,-1), area 1496mm2, adj f0,f1,f230,f232
  f232: plane 374x19mm, normal (0,0.71,0.71), area 10049.4mm2, adj f0,f1,f231,f233
  f233: plane 374x4mm, normal (0,0,1), area 1496mm2, adj f0,f1,f230,f232
  f234: plane 374x19mm, normal (0,-0.71,-0.71), area 10049.4mm2, adj f0,f1,f235,f237
  f235: plane 374x4mm, normal (0,0,-1), area 1496mm2, adj f0,f1,f234,f236
  f236: plane 374x19mm, normal (0,0.71,0.71), area 10049.4mm2, adj f0,f1,f235,f237
  f237: plane 374x4mm, normal (0,0,1), area 1496mm2, adj f0,f1,f234,f236
  f238: plane 374x19mm, normal (0,-0.71,-0.71), area 10049.4mm2, adj f0,f1,f239,f241
  f239: plane 374x4mm, normal (0,0,-1), area 1496mm2, adj f0,f1,f238,f240
  f240: plane 374x19mm, normal (0,0.71,0.71), area 10049.4mm2, adj f0,f1,f239,f241
  f241: plane 374x4mm, normal (0,0,1), area 1496mm2, adj f0,f1,f238,f240
  f242: plane 374x19mm, normal (0,-0.71,-0.71), area 10049.4mm2, adj f0,f1,f243,f245
  f243: plane 374x4mm, normal (0,0,-1), area 1496mm2, adj f0,f1,f242,f244
  f244: plane 374x19mm, normal (0,0.71,0.71), area 10049.4mm2, adj f0,f1,f243,f245
  f245: plane 374x4mm, normal (0,0,1), area 1496mm2, adj f0,f1,f242,f244
  f246: plane 374x19mm, normal (0,-0.71,-0.71), area 10049.4mm2, adj f0,f1,f247,f249
  f247: plane 374x4mm, normal (0,0,-1), area 1496mm2, adj f0,f1,f246,f248
  f248: plane 374x19mm, normal (0,0.71,0.71), area 10049.4mm2, adj f0,f1,f247,f249
  f249: plane 374x4mm, normal (0,0,1), area 1496mm2, adj f0,f1,f246,f248
  f250: plane 374x19mm, normal (0,-0.71,-0.71), area 10049.4mm2, adj f0,f1,f251,f253
  f251: plane 374x4mm, normal (0,0,-1), area 1496mm2, adj f0,f1,f250,f252
  f252: plane 374x19mm, normal (0,0.71,0.71), area 10049.4mm2, adj f0,f1,f251,f253
  f253: plane 374x4mm, normal (0,0,1), area 1496mm2, adj f0,f1,f250,f252
  f254: plane 374x19mm, normal (0,-0.71,-0.71), area 10049.4mm2, adj f0,f1,f255,f257
  f255: plane 374x4mm, normal (0,0,-1), area 1496mm2, adj f0,f1,f254,f256
  f256: plane 374x19mm, normal (0,0.71,0.71), area 10049.4mm2, adj f0,f1,f255,f257
  f257: plane 374x4mm, normal (0,0,1), area 1496mm2, adj f0,f1,f254,f256
  f258: plane 374x19mm, normal (0,-0.71,-0.71), area 10049.4mm2, adj f0,f1,f259,f261
  f259: plane 374x4mm, normal (0,0,-1), area 1496mm2, adj f0,f1,f258,f260
  f260: plane 374x19mm, normal (0,0.71,0.71), area 10049.4mm2, adj f0,f1,f259,f261
  f261: plane 374x4mm, normal (0,0,1), area 1496mm2, adj f0,f1,f258,f260
  f262: plane 374x19mm, normal (0,-0.71,-0.71), area 10049.4mm2, adj f0,f1,f263,f265
  f263: plane 374x4mm, normal (0,0,-1), area 1496mm2, adj f0,f1,f262,f264
  f264: plane 374x19mm, normal (0,0.71,0.71), area 10049.4mm2, adj f0,f1,f263,f265
  f265: plane 374x4mm, normal (0,0,1), area 1496mm2, adj f0,f1,f262,f264
  f266: plane 374x19mm, normal (0,-0.71,-0.71), area 10049.4mm2, adj f0,f1,f267,f269
  f267: plane 374x4mm, normal (0,0,-1), area 1496mm2, adj f0,f1,f266,f268
  f268: plane 374x19mm, normal (0,0.71,0.71), area 10049.4mm2, adj f0,f1,f267,f269
  f269: plane 374x4mm, normal (0,0,1), area 1496mm2, adj f0,f1,f266,f268
PLACE A t=(112.19,-1221.4,221.79)mm
PLACE B t=(112.19,-2999.4,221.79)mm
MATE parallel B.f8 <-> A.f8  axis (0,0,1) through (112.19,-1299.4,242.79)mm
MATE parallel A.f4 <-> B.f4  axis (-1,0,0) through (112.19,-861.4,232.29)mm
